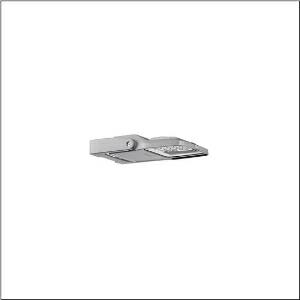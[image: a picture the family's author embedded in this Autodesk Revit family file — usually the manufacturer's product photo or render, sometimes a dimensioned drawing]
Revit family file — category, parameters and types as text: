
# Revit family: floodlight_fl_21_micro___pl33t_5xa7761a4f2a_f54c
name_source: partatom
category: Lighting Fixtures
units: mm (PartAtom-declared; Revit-internal decimal feet)

## family parameters
Cut with Voids When Loaded = No
Host = Face
Light Source = No
Part Type = Normal
Room Calculation Point = No
Round Connector Dimension = Use Diameter
Shared = No

## types (1)
- --- (1 x LED, 3050 lm, 23.1 W, 4000K)
    Apparent Load = 23 VA
    CIE Flux Codes = 26 75 99 100 100
    Color Rendering = 70
    Color Temperature = 4000K
    Default Elevation = 1800 mm
    Description = Floodlight FL 21 micro, floodlight, primary light control with lens, of PMMA, primary optical cover: protective disc, of toughened safety glass, transparent, light distribution: PL33T, light emission: direct distribution, installation type: surface-mounted, LED, High Power LED, rated luminous flux: 3.050lm, luminous efficacy: 132lm/W, light colour: 740, colour temperature: 4000K, control gear: ECG iQ, control: optimised constant luminous flux control (CLO 2.0), Desk-Remote (wireless, voltage-free reading and setting of iQ features in the workshop via application-optimized NFC function/RFID function), Light-Fading, Smart-Wire, Night-Set, Lumen-Switch, Temp-Guard, Auto-Match, with terminal, 6-pole, mains connection: 220..240V, AC, 50/60Hz, start of lifetime: 23W, end of lifetime: 24W, reduction: 11W, luminaire housing, of diecast aluminium, powder-coated, Siteco® metallic grey (DB 702S), corrosivity category C5 according to DIN EN ISO 12944, design bracket, of diecast aluminium, powder-coated, Siteco® metallic grey (DB 702S), protection rating (complete): IP66, insulation class (complete): insulation class II (safety insulation), certification: CE, protection symbol: D, impact resistance: IK07, permissible operating ambient temperature: -40..+40°C, permissible operating ambient temperature for outdoor applications: -40..+50°C, standard: DIN EN 12944, packaging unit: 1 piece

Light Distribution: PL33T
    Height = 65 mm
    Lamp = 1 x LED
    Lamp Light Flux = 3050 lm
    Lamp Power = 23.1 W
    Lamp count = 1
    Length = 312 mm
    Luminous efficacy = 132 lm/W
    Manufacturer = Siteco
    ModVariant = No
    Model = 5XA7761A4F2A
    Number of Poles = 1
    OnlyDefault = Yes
    Power Factor = 1
    Product Name = Floodlight FL 21 micro | PL33T
    Product group = floodlight | pylon top
    ProductGroupID = 6101
    Protection Class = Protection class II
    Protection Degree = IP 66
    RLX_Detail_Level = 1
    RlxData = <blob elided: 97197 chars, md5=04a911b7>
    Socket = socket
    Standby Power = 0 W
    System Light Flux = 3050 lm
    System Power = 23 W
    Type Comments = factory setting: luminous flux: 100 % | dim-lin: 254 | 455 mA
    Type Image = l_1006878.jpg
    URL = http://relux.com
    VarID = @adj_058243
    Voltage = 0 V
    Weight = 0.00 kg
    Width = 230 mm

## geometry (parser evidence)
native form markers: Blend x4, Sweep x11
no freeform markers — native parametric forms only
